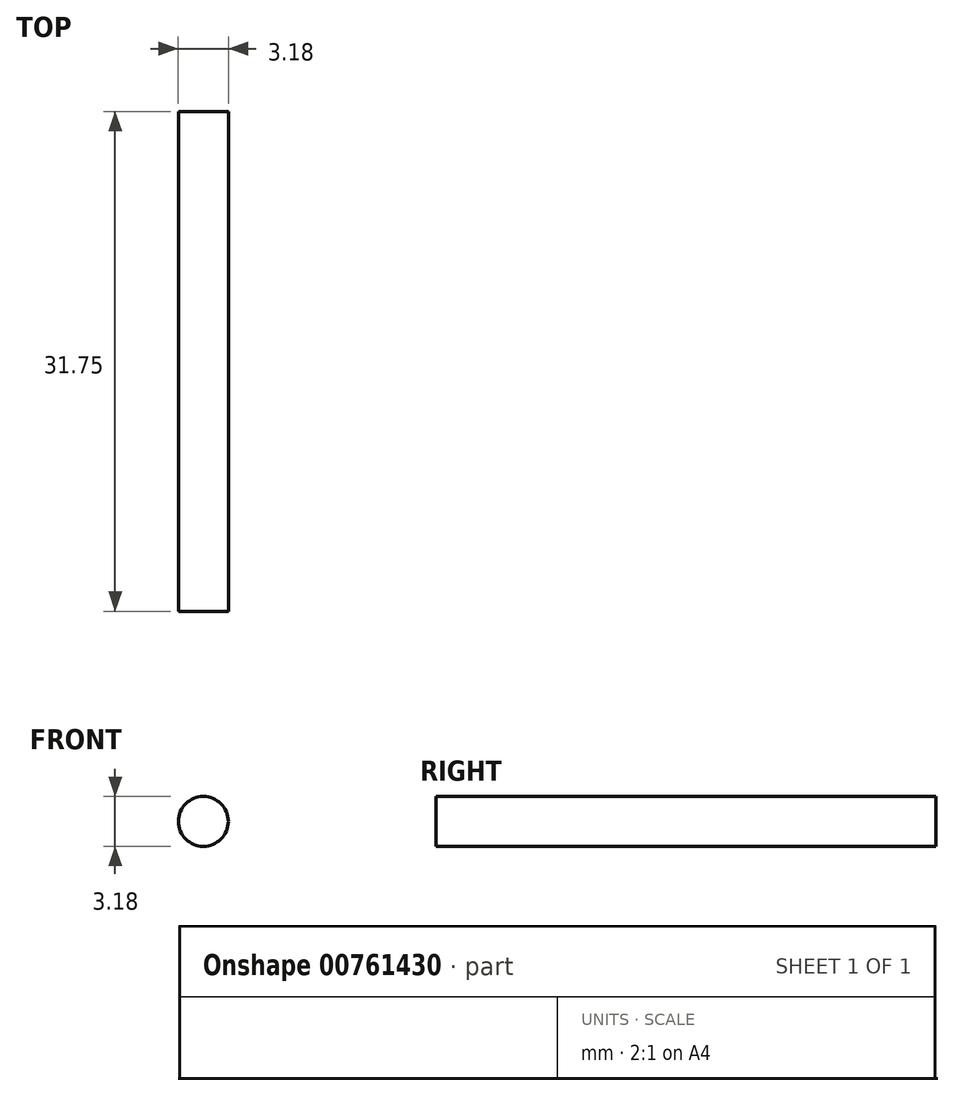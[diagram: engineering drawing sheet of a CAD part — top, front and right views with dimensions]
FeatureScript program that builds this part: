
annotation { "Feature Type Name" : "Feature", "Feature Type Description" : "" }
export const myFeature = defineFeature(function(context is Context, id is Id, definition is map)
    precondition{}
    {
        {
            var Q0;
            Q0=qCreatedBy(makeId("Front.planeOp"),FACE);
            var sketch = newSketch(context, id + "F0", { "sketchPlane" : qUnion([Q0])});
            skCircle(sketch, "E0", {"center": v(0, 0) * mm, "radius": 1.59 * mm});
            skSolve(sketch);
        }
        {
            var Q0;
            Q0=makeQuery(id+"F0.imprint","IMPRINT",FACE,{"disambiguationData":[TD([[makeQuery(id+"F0.imprint","IMPRINT",EDGE,{"derivedFrom":sQuery(id+"F0.wireOp",EDGE,"E0")}),1.0]])]});
            extrude(context, id + "F1", {"entities" : qUnion([Q0]), "depth" : 31.75 * mm, "offsetDistance" : 25.4 * mm});
        }
    });
